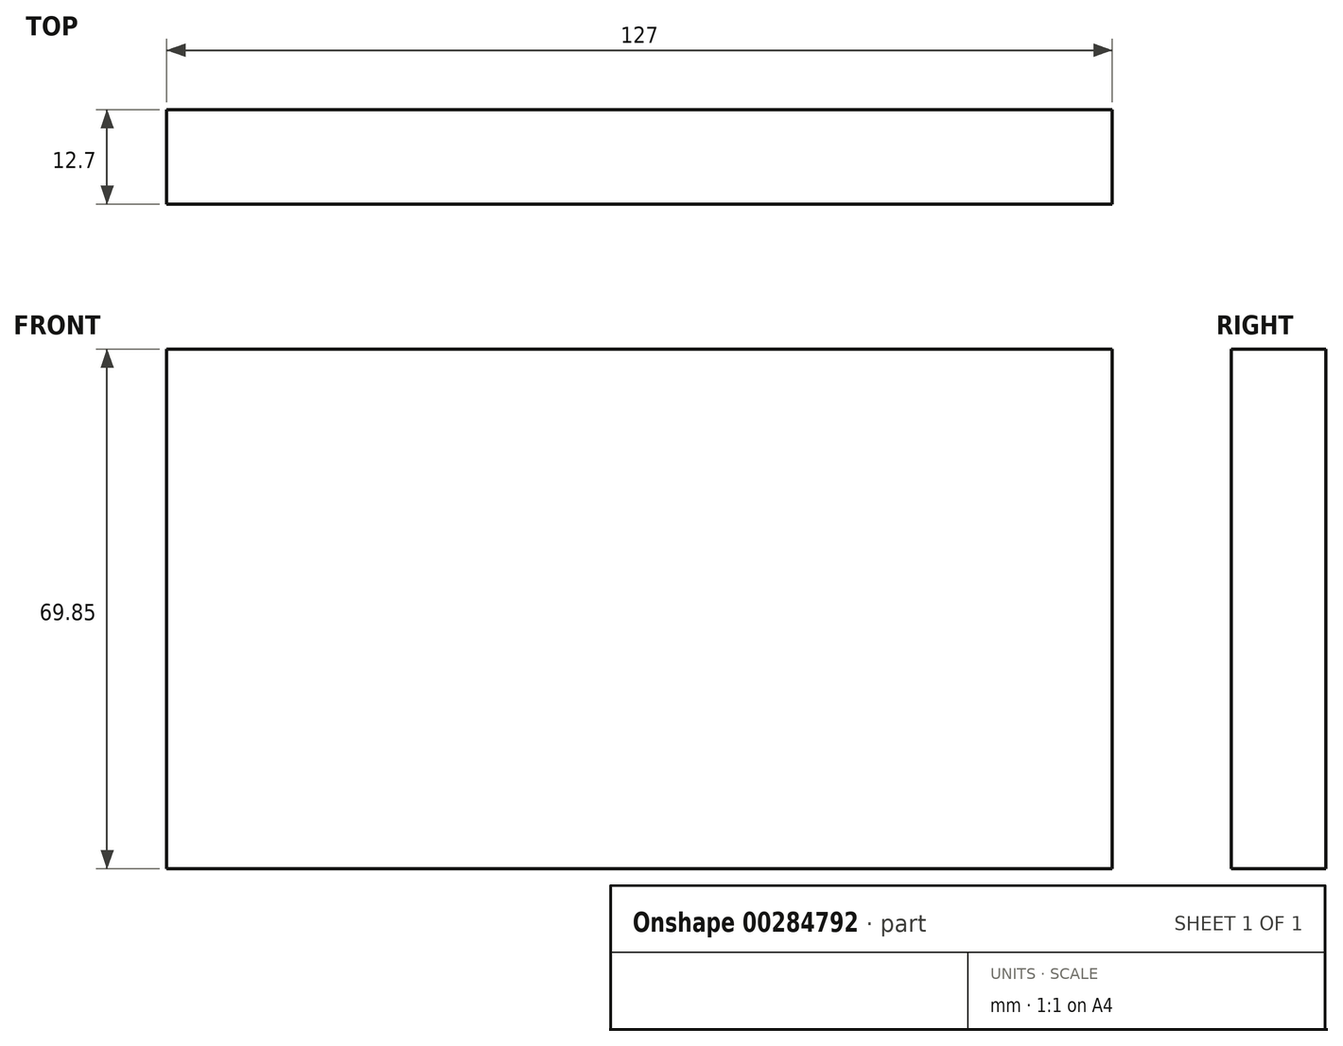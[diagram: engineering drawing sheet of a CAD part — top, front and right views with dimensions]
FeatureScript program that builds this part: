
annotation { "Feature Type Name" : "Feature", "Feature Type Description" : "" }
export const myFeature = defineFeature(function(context is Context, id is Id, definition is map)
    precondition{}
    {
        {
            var Q0;
            Q0=qCreatedBy(makeId("Front.planeOp"),FACE);
            var sketch = newSketch(context, id + "F0", { "sketchPlane" : qUnion([Q0])});
            skLineSegment(sketch, "E0.bottom", {"start": v(0, 0) * mm, "end": v(127, 0) * mm});
            skLineSegment(sketch, "E0.top", {"start": v(0, 69.85) * mm, "end": v(127, 69.85) * mm});
            skLineSegment(sketch, "E0.left", {"start": v(0, 0) * mm, "end": v(0, 69.85) * mm});
            skLineSegment(sketch, "E0.right", {"start": v(127, 0) * mm, "end": v(127, 69.85) * mm});
            skSolve(sketch);
        }
        {
            var Q0;
            Q0=makeQuery(id+"F0.imprint","IMPRINT",FACE,{"disambiguationData":[TD([[makeQuery(id+"F0.imprint","IMPRINT",EDGE,{"derivedFrom":sQuery(id+"F0.wireOp",EDGE,"E0.bottom")}),1.0]])]});
            extrude(context, id + "F1", {"entities" : qUnion([Q0]), "depth" : 12.7 * mm});
        }
    });
